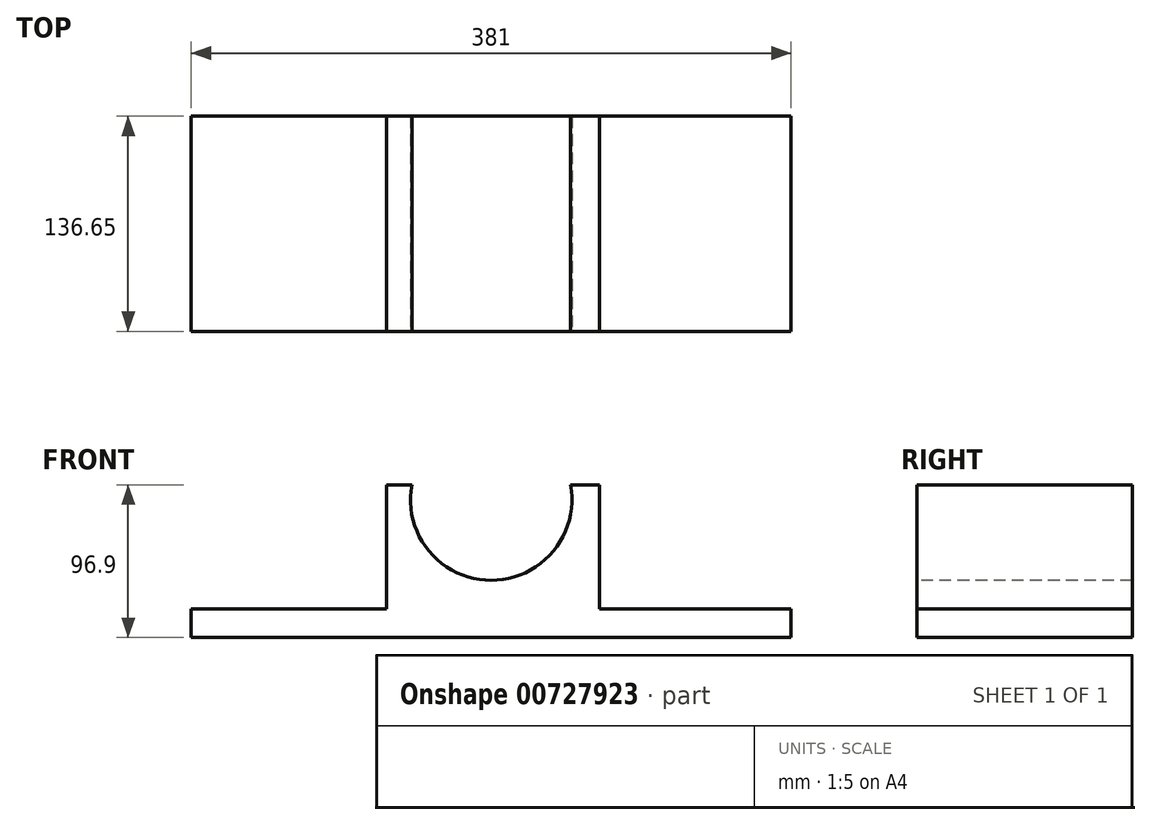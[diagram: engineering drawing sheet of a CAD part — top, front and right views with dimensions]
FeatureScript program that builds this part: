
annotation { "Feature Type Name" : "Feature", "Feature Type Description" : "" }
export const myFeature = defineFeature(function(context is Context, id is Id, definition is map)
    precondition{}
    {
        {
            var Q0;
            Q0=qCreatedBy(makeId("Front.planeOp"),FACE);
            var sketch = newSketch(context, id + "F0", { "sketchPlane" : qUnion([Q0])});
            skLineSegment(sketch, "E0.bottom", {"start": v(190.5, 48.45) * mm, "end": v(-190.5, 48.45) * mm});
            skLineSegment(sketch, "E0.top", {"start": v(190.5, -48.45) * mm, "end": v(-190.5, -48.45) * mm});
            skLineSegment(sketch, "E0.left", {"start": v(190.5, 48.45) * mm, "end": v(190.5, -48.45) * mm});
            skLineSegment(sketch, "E0.right", {"start": v(-190.5, 48.45) * mm, "end": v(-190.5, -48.45) * mm});
            skPoint(sketch, "E0.middle", {"position": v(0, 0) * mm});
            skArc(sketch, "E1", {"start": v(-50.4, 48.45) * mm, "mid": v(0, -12.27) * mm, "end": v(50.4, 48.45) * mm});
            skPoint(sketch, "E1.centerSnap0", {"position": v(0, 48.45) * mm});
            skLineSegment(sketch, "E2", {"start": v(68.68, 48.45) * mm, "end": v(68.68, -30.52) * mm});
            skLineSegment(sketch, "E3", {"start": v(68.68, -30.52) * mm, "end": v(190.5, -30.52) * mm});
            skLineSegment(sketch, "E4", {"start": v(-66.28, 48.45) * mm, "end": v(-66.28, -30.52) * mm});
            skLineSegment(sketch, "E5", {"start": v(-66.28, -30.52) * mm, "end": v(-190.5, -30.52) * mm});
            skSolve(sketch);
        }
        {
            var Q0;
            {var subQ1=sQuery(id+"F0.wireOp",EDGE,"E0.top");Q0=makeQuery(id+"F0.imprint","IMPRINT",FACE,{"disambiguationData":[TD([[makeQuery(id+"F0.imprint","IMPRINT",EDGE,{"derivedFrom":subQ1}),-1.0]])]});}
            var Q1;
            {var subQ0=sQuery(id+"F0.wireOp",EDGE,"E1");Q1=makeQuery(id+"F0.imprint","IMPRINT",FACE,{"disambiguationData":[TD([[makeQuery(id+"F0.imprint","IMPRINT",EDGE,{"derivedFrom":subQ0}),1.0]])]});}
            extrude(context, id + "F1", {"entities" : qUnion([Q0, Q1]), "oppositeDirection" : true, "depth" : 136.65 * mm, "offsetDistance" : 25.4 * mm});
        }
        {
            var Q0;
            {var subQ0=sQuery(id+"F0.wireOp",EDGE,"E1");Q0=makeQuery(id+"F0.imprint","IMPRINT",FACE,{"disambiguationData":[TD([[makeQuery(id+"F0.imprint","IMPRINT",EDGE,{"derivedFrom":subQ0}),1.0]])]});}
            extrude(context, id + "F2", {"entities" : qUnion([Q0]), "operationType" : NewBodyOperationType.REMOVE, "endBound" : BoundingType.THROUGH_ALL, "oppositeDirection" : true, "depth" : 25.4 * mm, "offsetDistance" : 25.4 * mm});
        }
        {
            var Q0;
            {var subQ3=sQuery(id+"F0.wireOp",EDGE,"E4");Q0=makeQuery(id+"F0.imprint","IMPRINT",FACE,{"disambiguationData":[TD([[makeQuery(id+"F0.imprint","IMPRINT",EDGE,{"derivedFrom":subQ3}),-1.0]])]});}
            var Q1;
            {var subQ3=sQuery(id+"F0.wireOp",EDGE,"E2");Q1=makeQuery(id+"F0.imprint","IMPRINT",FACE,{"disambiguationData":[TD([[makeQuery(id+"F0.imprint","IMPRINT",EDGE,{"derivedFrom":subQ3}),1.0]])]});}
            extrude(context, id + "F3", {"entities" : qUnion([Q0, Q1]), "operationType" : NewBodyOperationType.REMOVE, "endBound" : BoundingType.THROUGH_ALL, "oppositeDirection" : true, "depth" : 25.4 * mm, "offsetDistance" : 25.4 * mm});
        }
    });
